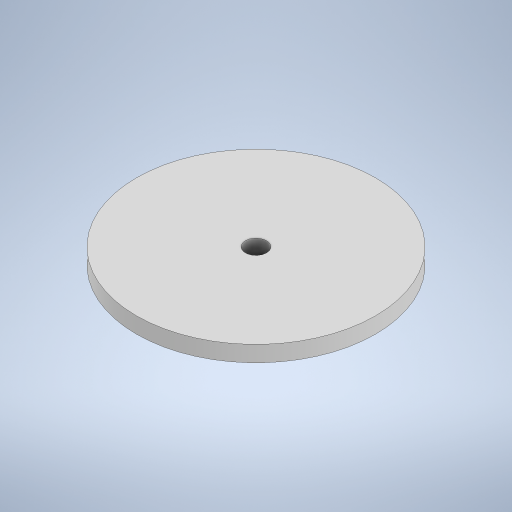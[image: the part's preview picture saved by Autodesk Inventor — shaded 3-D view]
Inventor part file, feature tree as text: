
AUTODESK INVENTOR PART (.ipt)
format: ipt  version: 2023 (Build 270158000, 158)  size: 219,648 bytes
history: native  units: mm
features: extrude x3, sketch x3, other x1
ambient origin geometry x8: Origin, YZ Plane, XZ Plane, XY Plane, X Axis, Y Axis, Z Axis, Center Point
bodies: Body1 (feature_tree)
feature tree (7):
  other  "ソリッド1"
  extrude  "押し出し1"  Depth=50.0mm
  extrude  "押し出し2"  Depth=6.0mm TaperAngle=0.0deg
  extrude  "押し出し3"  Depth=8.0mm
  sketch  "スケッチ1"
  sketch  "スケッチ2"
  sketch  "スケッチ3"
